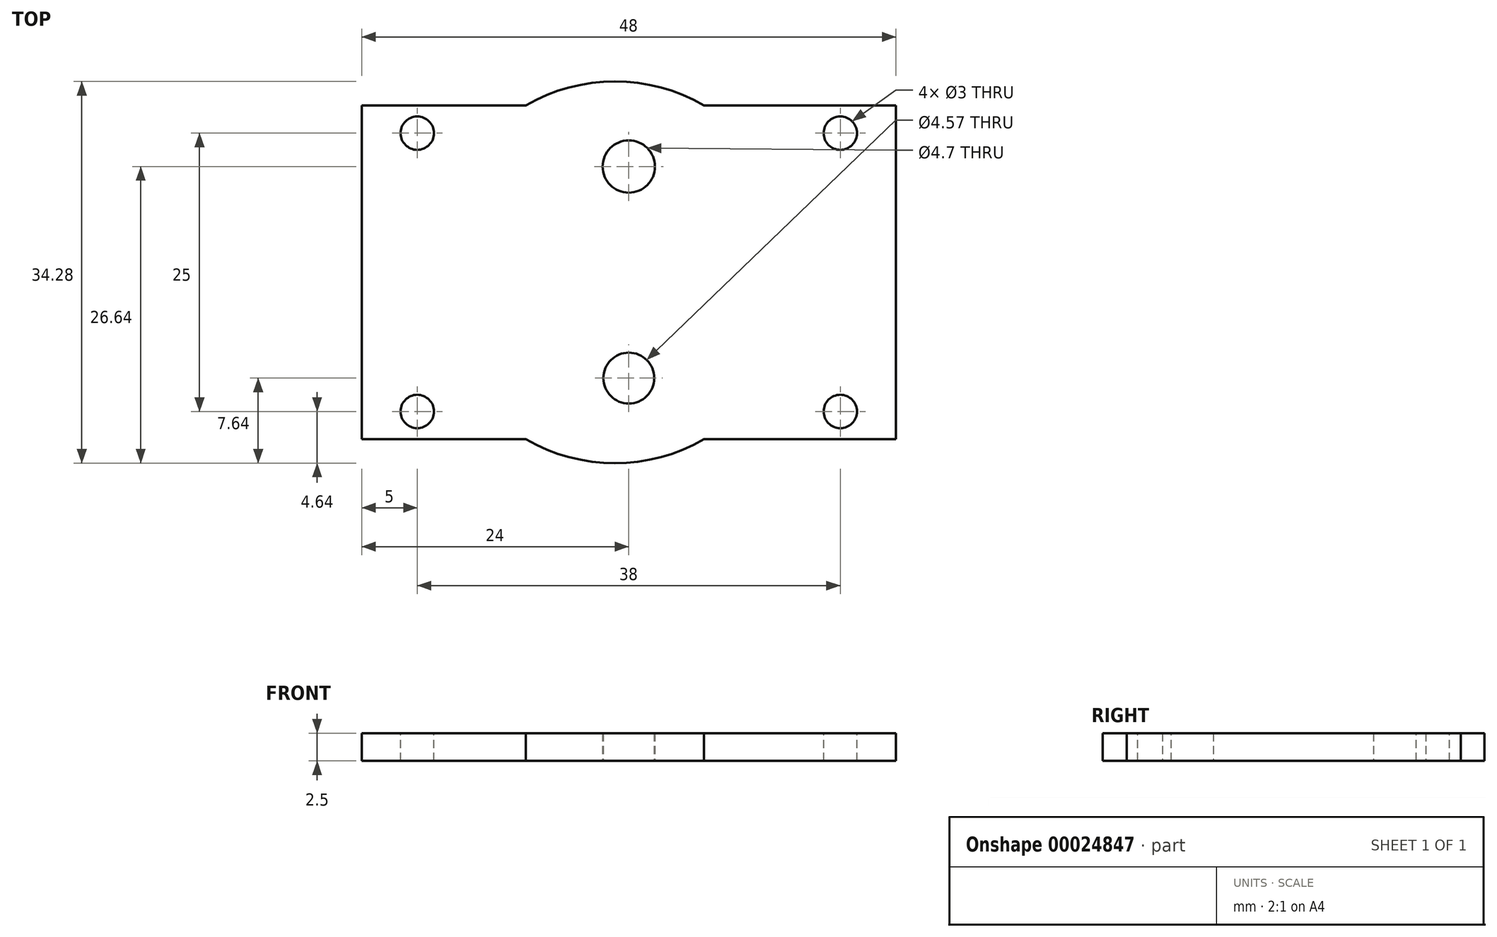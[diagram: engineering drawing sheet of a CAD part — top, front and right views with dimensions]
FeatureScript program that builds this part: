
annotation { "Feature Type Name" : "Feature", "Feature Type Description" : "" }
export const myFeature = defineFeature(function(context is Context, id is Id, definition is map)
    precondition{}
    {
        {
            var Q0;
            Q0=qCreatedBy(makeId("Top.planeOp"),FACE);
            var sketch = newSketch(context, id + "F0", { "sketchPlane" : qUnion([Q0])});
            skPoint(sketch, "E0.rect.middle", {"position": v(0, 0) * mm});
            skCircle(sketch, "E1", {"center": v(0, 0) * mm, "radius": 9.5 * mm, "construction": true});
            skCircle(sketch, "E2", {"center": v(0, 0) * mm, "radius": 14 * mm, "construction": true});
            skCircle(sketch, "E3", {"center": v(0, 9.5) * mm, "radius": 2.35 * mm});
            skCircle(sketch, "E4", {"center": v(0, -9.5) * mm, "radius": 2.28 * mm});
            skSolve(sketch);
        }
        {
            var Q0;
            Q0=qCreatedBy(makeId("Top.planeOp"),FACE);
            var sketch = newSketch(context, id + "F1", { "sketchPlane" : qUnion([Q0])});
            skLineSegment(sketch, "E5.rect.bottom", {"start": v(24, -15) * mm, "end": v(6.76, -15) * mm});
            skLineSegment(sketch, "E5.rect.top", {"start": v(24, 15) * mm, "end": v(6.76, 15) * mm});
            skLineSegment(sketch, "E5.rect.left", {"start": v(24, -15) * mm, "end": v(24, 15) * mm});
            skLineSegment(sketch, "E5.rect.right", {"start": v(-24, -15) * mm, "end": v(-24, 15) * mm});
            skPoint(sketch, "E5.rect.middle", {"position": v(0, 0) * mm});
            skArc(sketch, "E6", {"start": v(6.76, 15) * mm, "mid": v(-1.24, 17.14) * mm, "end": v(-9.25, 15) * mm});
            skArc(sketch, "E7.MirrorCS", {"start": v(6.76, -15) * mm, "mid": v(-1.24, -17.14) * mm, "end": v(-9.25, -15) * mm});
            skLineSegment(sketch, "E8.trimOffspring", {"start": v(-9.25, 15) * mm, "end": v(-24, 15) * mm});
            skLineSegment(sketch, "E9.trimOffspring", {"start": v(-9.25, -15) * mm, "end": v(-24, -15) * mm});
            skSolve(sketch);
        }
        {
            var Q0;
            Q0=qSketchRegion(id+"F1",true);
            extrude(context, id + "F2", {"entities" : qUnion([Q0]), "depth" : 2.5 * mm});
        }
        {
            var Q0;
            Q0=qSketchRegion(id+"F0",true);
            extrude(context, id + "F3", {"entities" : qUnion([Q0]), "operationType" : NewBodyOperationType.REMOVE, "endBound" : BoundingType.UP_TO_NEXT, "depth" : 25 * mm});
        }
        {
            var Q0;
            Q0=makeQuery(id+"F2.opExtrude","CAP_FACE",FACE,{"disambiguationData":[OSD([sQuery(id+"F1.wireOp",EDGE,"E5.rect.bottom"),sQuery(id+"F1.wireOp",EDGE,"E5.rect.top"),sQuery(id+"F1.wireOp",EDGE,"E5.rect.left"),sQuery(id+"F1.wireOp",EDGE,"E5.rect.right"),sQuery(id+"F1.wireOp",EDGE,"E6"),sQuery(id+"F1.wireOp",EDGE,"E7.MirrorCS"),sQuery(id+"F1.wireOp",EDGE,"E8.trimOffspring"),sQuery(id+"F1.wireOp",EDGE,"E9.trimOffspring")])],"isStart":false});
            var sketch = newSketch(context, id + "F4", { "sketchPlane" : qUnion([Q0])});
            skCircle(sketch, "E10", {"center": v(-19, 12.5) * mm, "radius": 1.5 * mm});
            skCircle(sketch, "E11.MirrorC", {"center": v(-19, -12.5) * mm, "radius": 1.5 * mm});
            skCircle(sketch, "E12.MirrorC", {"center": v(19, 12.5) * mm, "radius": 1.5 * mm});
            skCircle(sketch, "E13.MirrorC", {"center": v(19, -12.5) * mm, "radius": 1.5 * mm});
            skSolve(sketch);
        }
        {
            var Q0;
            Q0=qSketchRegion(id+"F4",true);
            extrude(context, id + "F5", {"entities" : qUnion([Q0]), "operationType" : NewBodyOperationType.REMOVE, "endBound" : BoundingType.UP_TO_NEXT, "oppositeDirection" : true, "depth" : 25 * mm});
        }
    });
